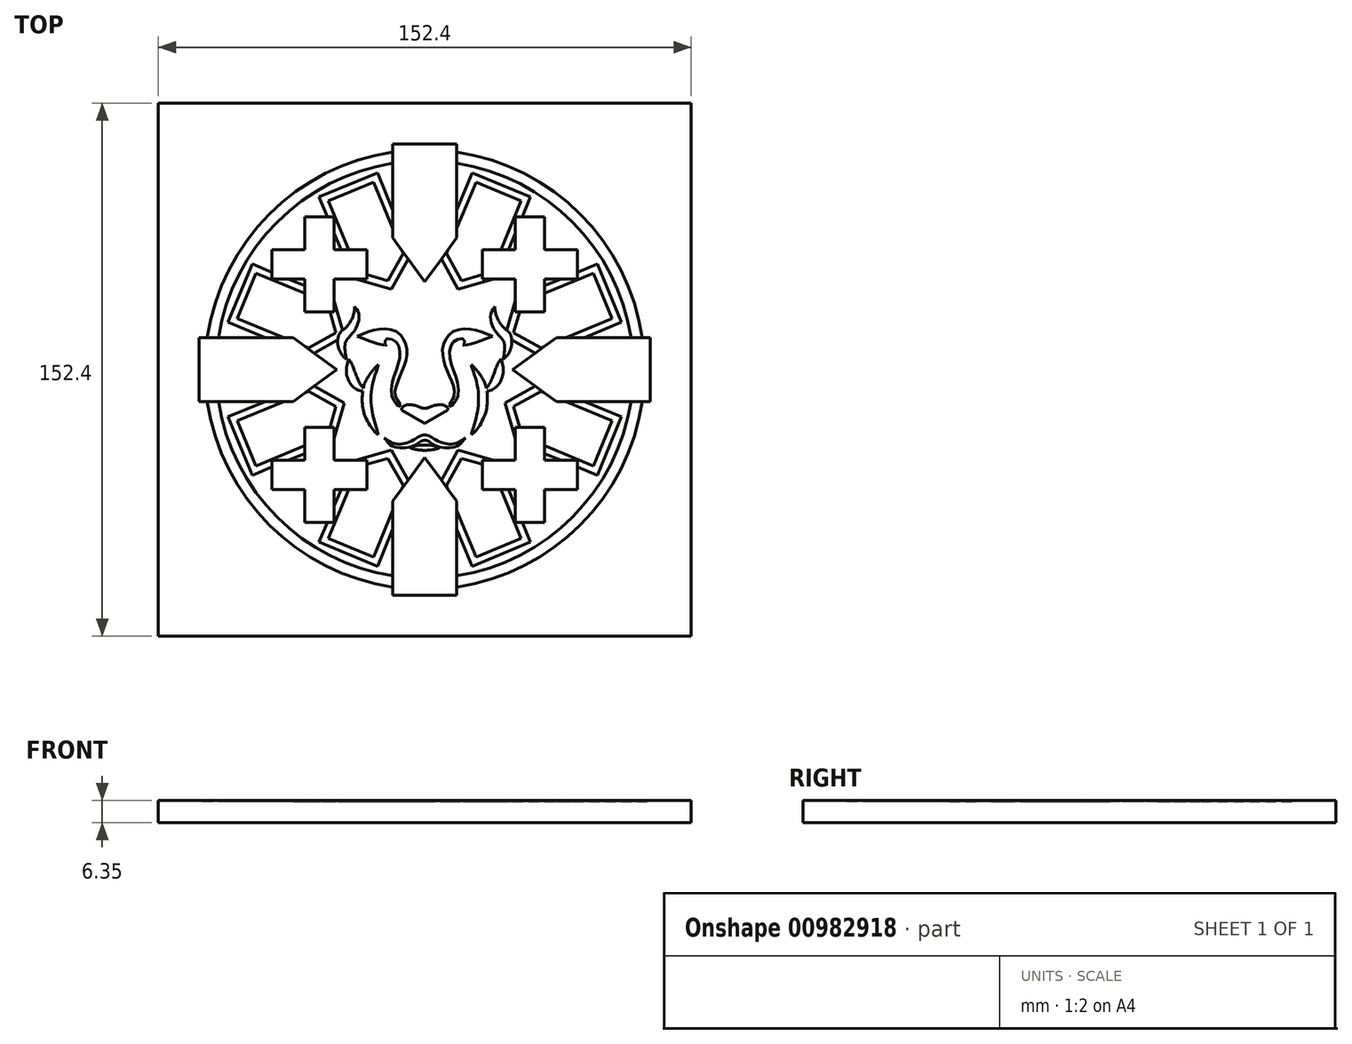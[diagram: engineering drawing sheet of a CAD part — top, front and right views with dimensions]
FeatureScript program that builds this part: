
annotation { "Feature Type Name" : "Feature", "Feature Type Description" : "" }
export const myFeature = defineFeature(function(context is Context, id is Id, definition is map)
    precondition{}
    {
        {
            assignVariable(context, id + "F0", {"name" : "depthArrowsHollow", "anyValue" : .2});
        }
        {
            assignVariable(context, id + "F1", {"name" : "depthArrowsSolid", "anyValue" : .4});
        }
        {
            assignVariable(context, id + "F2", {"name" : "depthCircle", "anyValue" : .2});
        }
        {
            assignVariable(context, id + "F3", {"name" : "depthCrosses", "anyValue" : .4});
        }
        {
            assignVariable(context, id + "F4", {"name" : "depthLion", "anyValue" : .4});
        }
        {
            var Q0;
            Q0=qCreatedBy(makeId("Top.planeOp"),FACE);
            var sketch = newSketch(context, id + "F5", { "sketchPlane" : qUnion([Q0])});
            skSolve(sketch);
        }
        {
            var Q0;
            Q0=qCreatedBy(makeId("Top.planeOp"),FACE);
            var sketch = newSketch(context, id + "F6", { "sketchPlane" : qUnion([Q0])});
            skCircle(sketch, "E0", {"center": v(81.98, 70.61) * mm, "radius": 59.7 * mm});
            skCircle(sketch, "E1", {"center": v(81.98, 70.61) * mm, "radius": 62.87 * mm});
            skPoint(sketch, "E2", {"position": v(0, 76.2) * mm});
            skPoint(sketch, "E3", {"position": v(75.25, 0) * mm});
            skLineSegment(sketch, "E4.bottom", {"start": v(5.78, -5.59) * mm, "end": v(158.18, -5.59) * mm});
            skLineSegment(sketch, "E4.top", {"start": v(5.78, 146.81) * mm, "end": v(158.18, 146.81) * mm});
            skLineSegment(sketch, "E4.left", {"start": v(5.78, -5.59) * mm, "end": v(5.78, 146.81) * mm});
            skLineSegment(sketch, "E4.right", {"start": v(158.18, -5.59) * mm, "end": v(158.18, 146.81) * mm});
            skSolve(sketch);
        }
        {
            var Q0;
            Q0=makeQuery(id+"F6.imprint","IMPRINT",FACE,{"disambiguationData":[TD([[makeQuery(id+"F6.imprint","IMPRINT",EDGE,{"derivedFrom":sQuery(id+"F6.wireOp",EDGE,"E1")}),-1.0]])]});
            var Q1;
            Q1=makeQuery(id+"F6.imprint","IMPRINT",FACE,{"disambiguationData":[TD([[makeQuery(id+"F6.imprint","IMPRINT",EDGE,{"derivedFrom":sQuery(id+"F6.wireOp",EDGE,"E0")}),-1.0]])]});
            var Q2;
            Q2=makeQuery(id+"F6.imprint","IMPRINT",FACE,{"disambiguationData":[TD([[makeQuery(id+"F6.imprint","IMPRINT",EDGE,{"derivedFrom":sQuery(id+"F6.wireOp",EDGE,"E0")}),1.0]])]});
            extrude(context, id + "F7", {"entities" : qUnion([Q0, Q1, Q2]), "oppositeDirection" : true, "depth" : 6.35 * mm, "offsetDistance" : 25.4 * mm});
        }
        {
            var Q0;
            Q0=makeQuery(id+"F6.imprint","IMPRINT",FACE,{"disambiguationData":[TD([[makeQuery(id+"F6.imprint","IMPRINT",EDGE,{"derivedFrom":sQuery(id+"F6.wireOp",EDGE,"E0")}),-1.0]])]});
            extrude(context, id + "F8", {"entities" : qUnion([Q0]), "operationType" : NewBodyOperationType.REMOVE, "oppositeDirection" : true, "depth" : (getVariable(context, 'depthCircle')) * mm, "offsetDistance" : 25.4 * mm});
        }
        {
            var Q0;
            Q0=qCreatedBy(makeId("Top.planeOp"),FACE);
            var sketch = newSketch(context, id + "F9", { "sketchPlane" : qUnion([Q0])});
            skLineSegment(sketch, "E5", {"start": v(17.47, 79.76) * mm, "end": v(17.47, 61.47) * mm});
            skLineSegment(sketch, "E6", {"start": v(17.47, 61.47) * mm, "end": v(44.33, 61.47) * mm});
            skLineSegment(sketch, "E7", {"start": v(44.33, 61.47) * mm, "end": v(56.84, 70.61) * mm});
            skLineSegment(sketch, "E8", {"start": v(56.84, 70.61) * mm, "end": v(44.33, 79.76) * mm});
            skLineSegment(sketch, "E9", {"start": v(44.33, 79.76) * mm, "end": v(17.47, 79.76) * mm});
            skCircle(sketch, "E10.0", {"center": v(81.98, 70.61) * mm, "radius": 62.87 * mm, "construction": true});
            skLineSegment(sketch, "E11", {"start": v(81.98, 70.61) * mm, "end": v(19.12, 70.61) * mm, "construction": true});
            skLineSegment(sketch, "E12.1.0", {"start": v(72.84, 32.96) * mm, "end": v(72.84, 6.1) * mm});
            skLineSegment(sketch, "E12.1.1", {"start": v(72.84, 6.1) * mm, "end": v(91.13, 6.1) * mm});
            skLineSegment(sketch, "E12.1.2", {"start": v(91.13, 6.1) * mm, "end": v(91.13, 32.96) * mm});
            skLineSegment(sketch, "E12.1.3", {"start": v(91.13, 32.96) * mm, "end": v(81.98, 45.47) * mm});
            skLineSegment(sketch, "E12.1.4", {"start": v(81.98, 45.47) * mm, "end": v(72.84, 32.96) * mm});
            skLineSegment(sketch, "E12.2.0", {"start": v(119.64, 61.47) * mm, "end": v(146.5, 61.47) * mm});
            skLineSegment(sketch, "E12.2.1", {"start": v(146.5, 61.47) * mm, "end": v(146.5, 79.76) * mm});
            skLineSegment(sketch, "E12.2.2", {"start": v(146.5, 79.76) * mm, "end": v(119.64, 79.76) * mm});
            skLineSegment(sketch, "E12.2.3", {"start": v(119.64, 79.76) * mm, "end": v(107.13, 70.61) * mm});
            skLineSegment(sketch, "E12.2.4", {"start": v(107.13, 70.61) * mm, "end": v(119.64, 61.47) * mm});
            skLineSegment(sketch, "E12.anchor1", {"start": v(81.98, 70.61) * mm, "end": v(17.47, 79.76) * mm, "construction": true});
            skLineSegment(sketch, "E12.anchor2", {"start": v(81.98, 70.61) * mm, "end": v(91.13, 135.13) * mm, "construction": true});
            skLineSegment(sketch, "E13.2.3.0", {"start": v(91.13, 108.27) * mm, "end": v(91.13, 135.13) * mm});
            skLineSegment(sketch, "E13.3.3.0", {"start": v(91.13, 135.13) * mm, "end": v(72.84, 135.13) * mm});
            skLineSegment(sketch, "E13.6.3.0", {"start": v(72.84, 135.13) * mm, "end": v(72.84, 108.27) * mm});
            skLineSegment(sketch, "E13.9.3.0", {"start": v(72.84, 108.27) * mm, "end": v(81.98, 95.76) * mm});
            skLineSegment(sketch, "E13.12.3.0", {"start": v(81.98, 95.76) * mm, "end": v(91.13, 108.27) * mm});
            skSolve(sketch);
        }
        {
            var Q0;
            Q0 = qSketchRegion(id + "F9", true);
            extrude(context, id + "F10", {"entities" : qUnion([Q0]), "operationType" : NewBodyOperationType.REMOVE, "oppositeDirection" : true, "depth" : (getVariable(context, 'depthArrowsSolid')) * mm, "offsetDistance" : 25.4 * mm});
        }
        {
            var Q0;
            Q0=qCreatedBy(makeId("Top.planeOp"),FACE);
            var sketch = newSketch(context, id + "F11", { "sketchPlane" : qUnion([Q0])});
            skLineSegment(sketch, "E14", {"start": v(47.7, 54.1) * mm, "end": v(56.07, 54.1) * mm});
            skLineSegment(sketch, "E15", {"start": v(56.07, 54.1) * mm, "end": v(56.07, 44.7) * mm});
            skLineSegment(sketch, "E16", {"start": v(56.07, 44.7) * mm, "end": v(65.47, 44.7) * mm});
            skLineSegment(sketch, "E17", {"start": v(65.47, 44.7) * mm, "end": v(65.47, 36.32) * mm});
            skLineSegment(sketch, "E18", {"start": v(65.47, 36.32) * mm, "end": v(56.07, 36.32) * mm});
            skLineSegment(sketch, "E19", {"start": v(56.07, 36.32) * mm, "end": v(56.07, 26.92) * mm});
            skLineSegment(sketch, "E20", {"start": v(56.07, 26.92) * mm, "end": v(47.7, 26.92) * mm});
            skLineSegment(sketch, "E21", {"start": v(47.7, 26.92) * mm, "end": v(47.7, 36.32) * mm});
            skLineSegment(sketch, "E22", {"start": v(47.7, 36.32) * mm, "end": v(38.3, 36.32) * mm});
            skLineSegment(sketch, "E23", {"start": v(38.3, 36.32) * mm, "end": v(38.3, 44.7) * mm});
            skLineSegment(sketch, "E24", {"start": v(38.3, 44.7) * mm, "end": v(47.7, 44.7) * mm});
            skLineSegment(sketch, "E25", {"start": v(47.7, 44.7) * mm, "end": v(47.7, 54.1) * mm});
            skCircle(sketch, "E26.0", {"center": v(81.98, 70.61) * mm, "radius": 62.87 * mm, "construction": true});
            skLineSegment(sketch, "E27.1.0", {"start": v(107.89, 26.92) * mm, "end": v(107.89, 36.32) * mm});
            skLineSegment(sketch, "E27.1.1", {"start": v(98.5, 36.32) * mm, "end": v(98.5, 44.7) * mm});
            skLineSegment(sketch, "E27.1.2", {"start": v(107.89, 44.7) * mm, "end": v(107.89, 54.1) * mm});
            skLineSegment(sketch, "E27.1.3", {"start": v(116.27, 54.1) * mm, "end": v(116.27, 44.7) * mm});
            skLineSegment(sketch, "E27.1.4", {"start": v(116.27, 36.32) * mm, "end": v(116.27, 26.92) * mm});
            skLineSegment(sketch, "E27.1.5", {"start": v(125.67, 44.7) * mm, "end": v(125.67, 36.32) * mm});
            skLineSegment(sketch, "E27.1.6", {"start": v(125.67, 36.32) * mm, "end": v(116.27, 36.32) * mm});
            skLineSegment(sketch, "E27.1.7", {"start": v(116.27, 44.7) * mm, "end": v(125.67, 44.7) * mm});
            skLineSegment(sketch, "E27.1.8", {"start": v(116.27, 26.92) * mm, "end": v(107.89, 26.92) * mm});
            skLineSegment(sketch, "E27.1.9", {"start": v(107.89, 54.1) * mm, "end": v(116.27, 54.1) * mm});
            skLineSegment(sketch, "E27.1.10", {"start": v(98.5, 44.7) * mm, "end": v(107.89, 44.7) * mm});
            skLineSegment(sketch, "E27.1.11", {"start": v(107.89, 36.32) * mm, "end": v(98.5, 36.32) * mm});
            skLineSegment(sketch, "E27.2.0", {"start": v(125.67, 96.52) * mm, "end": v(116.27, 96.52) * mm});
            skLineSegment(sketch, "E27.2.1", {"start": v(116.27, 87.12) * mm, "end": v(107.89, 87.12) * mm});
            skLineSegment(sketch, "E27.2.2", {"start": v(107.89, 96.52) * mm, "end": v(98.5, 96.52) * mm});
            skLineSegment(sketch, "E27.2.3", {"start": v(98.5, 104.9) * mm, "end": v(107.89, 104.9) * mm});
            skLineSegment(sketch, "E27.2.4", {"start": v(116.27, 104.9) * mm, "end": v(125.67, 104.9) * mm});
            skLineSegment(sketch, "E27.2.5", {"start": v(107.89, 114.3) * mm, "end": v(116.27, 114.3) * mm});
            skLineSegment(sketch, "E27.2.6", {"start": v(116.27, 114.3) * mm, "end": v(116.27, 104.9) * mm});
            skLineSegment(sketch, "E27.2.7", {"start": v(107.89, 104.9) * mm, "end": v(107.89, 114.3) * mm});
            skLineSegment(sketch, "E27.2.8", {"start": v(125.67, 104.9) * mm, "end": v(125.67, 96.52) * mm});
            skLineSegment(sketch, "E27.2.9", {"start": v(98.5, 96.52) * mm, "end": v(98.5, 104.9) * mm});
            skLineSegment(sketch, "E27.2.10", {"start": v(107.89, 87.12) * mm, "end": v(107.89, 96.52) * mm});
            skLineSegment(sketch, "E27.2.11", {"start": v(116.27, 96.52) * mm, "end": v(116.27, 87.12) * mm});
            skLineSegment(sketch, "E28.1.3.0", {"start": v(56.07, 114.3) * mm, "end": v(56.07, 104.9) * mm});
            skLineSegment(sketch, "E28.3.3.0", {"start": v(65.47, 104.9) * mm, "end": v(65.47, 96.52) * mm});
            skLineSegment(sketch, "E28.6.3.0", {"start": v(56.07, 96.52) * mm, "end": v(56.07, 87.12) * mm});
            skLineSegment(sketch, "E28.9.3.0", {"start": v(47.7, 87.12) * mm, "end": v(47.7, 96.52) * mm});
            skLineSegment(sketch, "E28.12.3.0", {"start": v(47.7, 104.9) * mm, "end": v(47.7, 114.3) * mm});
            skLineSegment(sketch, "E28.15.3.0", {"start": v(38.3, 96.52) * mm, "end": v(38.3, 104.9) * mm});
            skLineSegment(sketch, "E28.18.3.0", {"start": v(38.3, 104.9) * mm, "end": v(47.7, 104.9) * mm});
            skLineSegment(sketch, "E28.21.3.0", {"start": v(47.7, 96.52) * mm, "end": v(38.3, 96.52) * mm});
            skLineSegment(sketch, "E28.24.3.0", {"start": v(47.7, 114.3) * mm, "end": v(56.07, 114.3) * mm});
            skLineSegment(sketch, "E28.27.3.0", {"start": v(56.07, 87.12) * mm, "end": v(47.7, 87.12) * mm});
            skLineSegment(sketch, "E28.30.3.0", {"start": v(65.47, 96.52) * mm, "end": v(56.07, 96.52) * mm});
            skLineSegment(sketch, "E28.33.3.0", {"start": v(56.07, 104.9) * mm, "end": v(65.47, 104.9) * mm});
            skSolve(sketch);
        }
        {
            var Q0;
            Q0=makeQuery(id+"F11.imprint","IMPRINT",FACE,{"disambiguationData":[TD([[makeQuery(id+"F11.imprint","IMPRINT",EDGE,{"derivedFrom":sQuery(id+"F11.wireOp",EDGE,"E28.1.3.0")}),-1.0]])]});
            var Q1;
            Q1=makeQuery(id+"F11.imprint","IMPRINT",FACE,{"disambiguationData":[TD([[makeQuery(id+"F11.imprint","IMPRINT",EDGE,{"derivedFrom":sQuery(id+"F11.wireOp",EDGE,"E27.2.0")}),-1.0]])]});
            var Q2;
            Q2=makeQuery(id+"F11.imprint","IMPRINT",FACE,{"disambiguationData":[TD([[makeQuery(id+"F11.imprint","IMPRINT",EDGE,{"derivedFrom":sQuery(id+"F11.wireOp",EDGE,"E27.1.0")}),-1.0]])]});
            var Q3;
            Q3=makeQuery(id+"F11.imprint","IMPRINT",FACE,{"disambiguationData":[TD([[makeQuery(id+"F11.imprint","IMPRINT",EDGE,{"derivedFrom":sQuery(id+"F11.wireOp",EDGE,"E14")}),-1.0]])]});
            var Q4;
            Q4=makeQuery(id+"F9.imprint","IMPRINT",FACE,{"disambiguationData":[TD([[makeQuery(id+"F9.imprint","IMPRINT",EDGE,{"derivedFrom":sQuery(id+"F9.wireOp",EDGE,"E5")}),1.0]])]});
            var Q5;
            Q5=makeQuery(id+"F9.imprint","IMPRINT",FACE,{"disambiguationData":[TD([[makeQuery(id+"F9.imprint","IMPRINT",EDGE,{"derivedFrom":sQuery(id+"F9.wireOp",EDGE,"E13.2.3.0")}),1.0]])]});
            var Q6;
            Q6=makeQuery(id+"F9.imprint","IMPRINT",FACE,{"disambiguationData":[TD([[makeQuery(id+"F9.imprint","IMPRINT",EDGE,{"derivedFrom":sQuery(id+"F9.wireOp",EDGE,"E12.2.0")}),1.0]])]});
            var Q7;
            Q7=makeQuery(id+"F9.imprint","IMPRINT",FACE,{"disambiguationData":[TD([[makeQuery(id+"F9.imprint","IMPRINT",EDGE,{"derivedFrom":sQuery(id+"F9.wireOp",EDGE,"E12.1.0")}),1.0]])]});
            extrude(context, id + "F12", {"entities" : qUnion([Q0, Q1, Q2, Q3, Q4, Q5, Q6, Q7]), "operationType" : NewBodyOperationType.REMOVE, "oppositeDirection" : true, "depth" : (getVariable(context, 'depthCrosses')) * mm, "offsetDistance" : 25.4 * mm});
        }
        {
            var Q0;
            Q0=qCreatedBy(makeId("Top.planeOp"),FACE);
            var sketch = newSketch(context, id + "F13", { "sketchPlane" : qUnion([Q0])});
            skLineSegment(sketch, "E29", {"start": v(25.73, 57.07) * mm, "end": v(48.9, 66.67) * mm});
            skLineSegment(sketch, "E30", {"start": v(48.9, 66.67) * mm, "end": v(58.98, 61.09) * mm});
            skLineSegment(sketch, "E31", {"start": v(58.98, 61.09) * mm, "end": v(55.8, 50.01) * mm});
            skLineSegment(sketch, "E32", {"start": v(55.8, 50.01) * mm, "end": v(32.63, 40.41) * mm});
            skLineSegment(sketch, "E33", {"start": v(32.63, 40.41) * mm, "end": v(25.73, 57.07) * mm});
            skCircle(sketch, "E34.0", {"center": v(81.98, 70.61) * mm, "radius": 62.87 * mm, "construction": true});
            skLineSegment(sketch, "E35", {"start": v(81.98, 70.61) * mm, "end": v(29.18, 48.74) * mm, "construction": true});
            skLineSegment(sketch, "E36", {"start": v(81.98, 70.61) * mm, "end": v(19.12, 70.61) * mm, "construction": true});
            skLineSegment(sketch, "E37.0", {"start": v(48.78, 64.42) * mm, "end": v(56.59, 60.1) * mm});
            skLineSegment(sketch, "E37.1", {"start": v(28.39, 55.97) * mm, "end": v(48.78, 64.42) * mm});
            skLineSegment(sketch, "E37.2", {"start": v(56.59, 60.1) * mm, "end": v(54.13, 51.51) * mm});
            skLineSegment(sketch, "E37.3", {"start": v(54.13, 51.51) * mm, "end": v(33.73, 43.07) * mm});
            skLineSegment(sketch, "E37.4", {"start": v(33.73, 43.07) * mm, "end": v(28.39, 55.97) * mm});
            skLineSegment(sketch, "E38.1.0", {"start": v(54.44, 22.36) * mm, "end": v(62.88, 42.76) * mm});
            skLineSegment(sketch, "E38.1.1", {"start": v(51.78, 21.26) * mm, "end": v(61.38, 44.44) * mm});
            skLineSegment(sketch, "E38.1.2", {"start": v(75.79, 37.4) * mm, "end": v(67.34, 17.02) * mm});
            skLineSegment(sketch, "E38.1.3", {"start": v(78.04, 37.54) * mm, "end": v(68.44, 14.36) * mm});
            skLineSegment(sketch, "E38.1.4", {"start": v(67.34, 17.02) * mm, "end": v(54.44, 22.36) * mm});
            skLineSegment(sketch, "E38.1.5", {"start": v(68.44, 14.36) * mm, "end": v(51.78, 21.26) * mm});
            skLineSegment(sketch, "E38.1.6", {"start": v(62.88, 42.76) * mm, "end": v(71.46, 45.22) * mm});
            skLineSegment(sketch, "E38.1.7", {"start": v(61.38, 44.44) * mm, "end": v(72.46, 47.61) * mm});
            skLineSegment(sketch, "E38.1.8", {"start": v(71.46, 45.22) * mm, "end": v(75.79, 37.4) * mm});
            skLineSegment(sketch, "E38.1.9", {"start": v(72.46, 47.61) * mm, "end": v(78.04, 37.54) * mm});
            skLineSegment(sketch, "E38.2.0", {"start": v(96.62, 17.02) * mm, "end": v(88.17, 37.4) * mm});
            skLineSegment(sketch, "E38.2.1", {"start": v(95.52, 14.36) * mm, "end": v(85.92, 37.54) * mm});
            skLineSegment(sketch, "E38.2.2", {"start": v(101.08, 42.76) * mm, "end": v(109.53, 22.36) * mm});
            skLineSegment(sketch, "E38.2.3", {"start": v(102.58, 44.44) * mm, "end": v(112.18, 21.26) * mm});
            skLineSegment(sketch, "E38.2.4", {"start": v(109.53, 22.36) * mm, "end": v(96.62, 17.02) * mm});
            skLineSegment(sketch, "E38.2.5", {"start": v(112.18, 21.26) * mm, "end": v(95.52, 14.36) * mm});
            skLineSegment(sketch, "E38.2.6", {"start": v(88.17, 37.4) * mm, "end": v(92.5, 45.22) * mm});
            skLineSegment(sketch, "E38.2.7", {"start": v(85.92, 37.54) * mm, "end": v(91.5, 47.61) * mm});
            skLineSegment(sketch, "E38.2.8", {"start": v(92.5, 45.22) * mm, "end": v(101.08, 42.76) * mm});
            skLineSegment(sketch, "E38.2.9", {"start": v(91.5, 47.61) * mm, "end": v(102.58, 44.44) * mm});
            skLineSegment(sketch, "E39.1.3.0", {"start": v(130.23, 43.07) * mm, "end": v(109.84, 51.51) * mm});
            skLineSegment(sketch, "E39.3.3.0", {"start": v(131.33, 40.41) * mm, "end": v(108.15, 50.01) * mm});
            skLineSegment(sketch, "E39.6.3.0", {"start": v(115.18, 64.42) * mm, "end": v(135.58, 55.97) * mm});
            skLineSegment(sketch, "E39.9.3.0", {"start": v(115.06, 66.67) * mm, "end": v(138.23, 57.07) * mm});
            skLineSegment(sketch, "E39.12.3.0", {"start": v(135.58, 55.97) * mm, "end": v(130.23, 43.07) * mm});
            skLineSegment(sketch, "E39.15.3.0", {"start": v(138.23, 57.07) * mm, "end": v(131.33, 40.41) * mm});
            skLineSegment(sketch, "E39.18.3.0", {"start": v(109.84, 51.51) * mm, "end": v(107.38, 60.1) * mm});
            skLineSegment(sketch, "E39.21.3.0", {"start": v(108.15, 50.01) * mm, "end": v(104.98, 61.09) * mm});
            skLineSegment(sketch, "E39.24.3.0", {"start": v(107.38, 60.1) * mm, "end": v(115.18, 64.42) * mm});
            skLineSegment(sketch, "E39.27.3.0", {"start": v(104.98, 61.09) * mm, "end": v(115.06, 66.67) * mm});
            skLineSegment(sketch, "E39.1.4.0", {"start": v(135.58, 85.25) * mm, "end": v(115.18, 76.8) * mm});
            skLineSegment(sketch, "E39.3.4.0", {"start": v(138.23, 84.15) * mm, "end": v(115.06, 74.55) * mm});
            skLineSegment(sketch, "E39.6.4.0", {"start": v(109.84, 89.71) * mm, "end": v(130.23, 98.16) * mm});
            skLineSegment(sketch, "E39.9.4.0", {"start": v(108.15, 91.21) * mm, "end": v(131.33, 100.81) * mm});
            skLineSegment(sketch, "E39.12.4.0", {"start": v(130.23, 98.16) * mm, "end": v(135.58, 85.25) * mm});
            skLineSegment(sketch, "E39.15.4.0", {"start": v(131.33, 100.81) * mm, "end": v(138.23, 84.15) * mm});
            skLineSegment(sketch, "E39.18.4.0", {"start": v(115.18, 76.8) * mm, "end": v(107.38, 81.13) * mm});
            skLineSegment(sketch, "E39.21.4.0", {"start": v(115.06, 74.55) * mm, "end": v(104.98, 80.14) * mm});
            skLineSegment(sketch, "E39.24.4.0", {"start": v(107.38, 81.13) * mm, "end": v(109.84, 89.71) * mm});
            skLineSegment(sketch, "E39.27.4.0", {"start": v(104.98, 80.14) * mm, "end": v(108.15, 91.21) * mm});
            skLineSegment(sketch, "E39.1.5.0", {"start": v(109.53, 118.86) * mm, "end": v(101.08, 98.47) * mm});
            skLineSegment(sketch, "E39.3.5.0", {"start": v(112.18, 119.96) * mm, "end": v(102.58, 96.79) * mm});
            skLineSegment(sketch, "E39.6.5.0", {"start": v(88.17, 103.81) * mm, "end": v(96.62, 124.2) * mm});
            skLineSegment(sketch, "E39.9.5.0", {"start": v(85.92, 103.69) * mm, "end": v(95.52, 126.86) * mm});
            skLineSegment(sketch, "E39.12.5.0", {"start": v(96.62, 124.2) * mm, "end": v(109.53, 118.86) * mm});
            skLineSegment(sketch, "E39.15.5.0", {"start": v(95.52, 126.86) * mm, "end": v(112.18, 119.96) * mm});
            skLineSegment(sketch, "E39.18.5.0", {"start": v(101.08, 98.47) * mm, "end": v(92.5, 96) * mm});
            skLineSegment(sketch, "E39.21.5.0", {"start": v(102.58, 96.79) * mm, "end": v(91.5, 93.6) * mm});
            skLineSegment(sketch, "E39.24.5.0", {"start": v(92.5, 96) * mm, "end": v(88.17, 103.81) * mm});
            skLineSegment(sketch, "E39.27.5.0", {"start": v(91.5, 93.6) * mm, "end": v(85.92, 103.69) * mm});
            skLineSegment(sketch, "E39.1.6.0", {"start": v(67.34, 124.2) * mm, "end": v(75.79, 103.81) * mm});
            skLineSegment(sketch, "E39.3.6.0", {"start": v(68.44, 126.86) * mm, "end": v(78.04, 103.69) * mm});
            skLineSegment(sketch, "E39.6.6.0", {"start": v(62.88, 98.47) * mm, "end": v(54.44, 118.86) * mm});
            skLineSegment(sketch, "E39.9.6.0", {"start": v(61.38, 96.79) * mm, "end": v(51.78, 119.96) * mm});
            skLineSegment(sketch, "E39.12.6.0", {"start": v(54.44, 118.86) * mm, "end": v(67.34, 124.2) * mm});
            skLineSegment(sketch, "E39.15.6.0", {"start": v(51.78, 119.96) * mm, "end": v(68.44, 126.86) * mm});
            skLineSegment(sketch, "E39.18.6.0", {"start": v(75.79, 103.81) * mm, "end": v(71.46, 96) * mm});
            skLineSegment(sketch, "E39.21.6.0", {"start": v(78.04, 103.69) * mm, "end": v(72.46, 93.6) * mm});
            skLineSegment(sketch, "E39.24.6.0", {"start": v(71.46, 96) * mm, "end": v(62.88, 98.47) * mm});
            skLineSegment(sketch, "E39.27.6.0", {"start": v(72.46, 93.6) * mm, "end": v(61.38, 96.79) * mm});
            skLineSegment(sketch, "E39.1.7.0", {"start": v(33.73, 98.16) * mm, "end": v(54.13, 89.71) * mm});
            skLineSegment(sketch, "E39.3.7.0", {"start": v(32.63, 100.81) * mm, "end": v(55.8, 91.21) * mm});
            skLineSegment(sketch, "E39.6.7.0", {"start": v(48.78, 76.8) * mm, "end": v(28.39, 85.25) * mm});
            skLineSegment(sketch, "E39.9.7.0", {"start": v(48.9, 74.55) * mm, "end": v(25.73, 84.15) * mm});
            skLineSegment(sketch, "E39.12.7.0", {"start": v(28.39, 85.25) * mm, "end": v(33.73, 98.16) * mm});
            skLineSegment(sketch, "E39.15.7.0", {"start": v(25.73, 84.15) * mm, "end": v(32.63, 100.81) * mm});
            skLineSegment(sketch, "E39.18.7.0", {"start": v(54.13, 89.71) * mm, "end": v(56.59, 81.13) * mm});
            skLineSegment(sketch, "E39.21.7.0", {"start": v(55.8, 91.21) * mm, "end": v(58.98, 80.14) * mm});
            skLineSegment(sketch, "E39.24.7.0", {"start": v(56.59, 81.13) * mm, "end": v(48.78, 76.8) * mm});
            skLineSegment(sketch, "E39.27.7.0", {"start": v(58.98, 80.14) * mm, "end": v(48.9, 74.55) * mm});
            skSolve(sketch);
        }
        {
            var Q0;
            Q0 = qSketchRegion(id + "F13", true);
            extrude(context, id + "F14", {"entities" : qUnion([Q0]), "operationType" : NewBodyOperationType.REMOVE, "oppositeDirection" : true, "depth" : (getVariable(context, 'depthArrowsHollow')) * mm, "offsetDistance" : 25.4 * mm});
        }
        {
            var Q0;
            Q0=qCreatedBy(makeId("Top.planeOp"),FACE);
            var sketch = newSketch(context, id + "F15", { "sketchPlane" : qUnion([Q0])});
            skLineSegment(sketch, "E40", {"start": v(81.98, 146.81) * mm, "end": v(81.98, -5.59) * mm, "construction": true});
            skFitSpline(sketch, "E41", {"points": [v(61.94, 88.6) * mm, v(61.72, 86.72) * mm, v(61.16, 85.16) * mm, v(60.37, 83.77) * mm, v(59.24, 82.46) * mm, v(57.86, 81.25) * mm, v(57.15, 79.47) * mm, v(57.17, 77.48) * mm, v(58.02, 75.2) * mm, v(59.6, 73.57) * mm], "startDerivative": vector(0.03, -23.03) * mm, "endDerivative": vector(20.52, -14.62) * mm});
            skFitSpline(sketch, "E42", {"points": [v(61.94, 88.6) * mm, v(63.17, 85.4) * mm, v(61.82, 81.66) * mm, v(59.62, 79.03) * mm, v(59.15, 77.49) * mm, v(59.2, 75.8) * mm, v(59.6, 73.57) * mm], "startDerivative": vector(15.35, -14.7) * mm, "endDerivative": vector(4.08, -12.06) * mm});
            skFitSpline(sketch, "E43", {"points": [v(60.19, 73.61) * mm, v(59.65, 71.61) * mm, v(59.62, 69.33) * mm, v(60.38, 67.13) * mm, v(61.9, 65.3) * mm, v(63.68, 64.54) * mm, v(65.16, 64.56) * mm], "startDerivative": vector(-2.41, -6.85) * mm, "endDerivative": vector(6.9, 1.88) * mm});
            skFitSpline(sketch, "E44", {"points": [v(60.19, 73.61) * mm, v(60.88, 72.65) * mm, v(61.49, 71.36) * mm, v(62.1, 69.66) * mm, v(62.83, 67.93) * mm, v(63.58, 66.36) * mm, v(64.31, 65.39) * mm, v(65.16, 64.56) * mm], "startDerivative": vector(5.66, -7.2) * mm, "endDerivative": vector(1.92, -1.83) * mm});
            skFitSpline(sketch, "E45", {"points": [v(62.61, 80.06) * mm, v(65.49, 81.37) * mm, v(68.65, 82.13) * mm, v(71.55, 82.19) * mm, v(74.34, 81.17) * mm, v(75.9, 79.37) * mm, v(76.8, 77.03) * mm, v(76.77, 74.1) * mm, v(76, 71.47) * mm, v(74.87, 68.71) * mm, v(73.97, 66.34) * mm, v(73.44, 64.03) * mm, v(74.08, 61.94) * mm, v(74.86, 60.7) * mm, v(74.91, 60.03) * mm], "startDerivative": vector(34.56, 17.51) * mm, "endDerivative": vector(-4.35, -17.1) * mm});
            skFitSpline(sketch, "E46", {"points": [v(74.91, 60.03) * mm, v(74.28, 60.16) * mm, v(73.28, 61.53) * mm, v(72.44, 63.44) * mm, v(72.55, 66.35) * mm, v(73.32, 69.02) * mm, v(74.22, 71.68) * mm, v(74.84, 74.24) * mm, v(74.73, 76.7) * mm, v(74.03, 78.22) * mm, v(72.94, 79.03) * mm, v(71.18, 79.46) * mm, v(70.7, 78.99) * mm, v(70.58, 78.47) * mm, v(70.7, 77.97) * mm, v(70.9, 77.62) * mm, v(70.93, 77.54) * mm, v(70.82, 77.54) * mm, v(69.56, 77.7) * mm, v(68.42, 78) * mm, v(67.1, 78.45) * mm, v(65.18, 79.17) * mm, v(62.61, 80.06) * mm], "startDerivative": vector(-21.39, -1.32) * mm, "endDerivative": vector(-39.34, 13.04) * mm});
            skFitSpline(sketch, "E47", {"points": [v(68.72, 72) * mm, v(68.33, 70.7) * mm, v(67.57, 68.42) * mm, v(66.9, 65.8) * mm, v(66.58, 62.86) * mm, v(66.73, 60.18) * mm, v(67.07, 57.9) * mm, v(67.64, 55.51) * mm, v(68.31, 53.3) * mm, v(68.71, 52) * mm], "startDerivative": vector(-6.69, -19.51) * mm, "endDerivative": vector(4.6, -12.75) * mm});
            skFitSpline(sketch, "E48", {"points": [v(68.71, 52) * mm, v(67.56, 52.94) * mm, v(65.3, 56.48) * mm, v(64.22, 59.9) * mm, v(64.12, 63.32) * mm, v(64.79, 66.64) * mm, v(66.23, 69.26) * mm, v(67.6, 71) * mm, v(68.72, 72) * mm], "startDerivative": vector(-13.48, 8.73) * mm, "endDerivative": vector(15.01, 11.43) * mm});
            skFitSpline(sketch, "E49", {"points": [v(70.36, 51.06) * mm, v(70.67, 50.78) * mm, v(70.99, 50.37) * mm, v(71.26, 49.96) * mm, v(71.6, 49.53) * mm, v(72.75, 48.76) * mm, v(74.23, 48.32) * mm, v(76.3, 48.28) * mm, v(78.03, 48.59) * mm, v(79.36, 49.08) * mm, v(80.25, 49.7) * mm, v(80.77, 50.1) * mm, v(81.26, 50.3) * mm, v(81.68, 50.34) * mm, v(81.98, 50.34) * mm], "startDerivative": vector(6.26, -5.13) * mm, "endDerivative": vector(6.83, -0.1) * mm});
            skFitSpline(sketch, "E50", {"points": [v(70.36, 51.06) * mm, v(70.75, 50.83) * mm, v(71.26, 50.5) * mm, v(72.1, 50) * mm, v(73, 49.58) * mm, v(74.2, 49.32) * mm, v(75.52, 49.35) * mm, v(77.03, 49.74) * mm, v(78.68, 50.44) * mm, v(79.85, 51.2) * mm, v(80.76, 51.7) * mm, v(81.5, 51.89) * mm, v(81.98, 51.9) * mm], "startDerivative": vector(6.78, -3.92) * mm, "endDerivative": vector(7.94, 0.08) * mm});
            skFitSpline(sketch, "E51", {"points": [v(75.37, 59.05) * mm, v(75.43, 59.4) * mm, v(75.72, 59.93) * mm, v(76.23, 60.35) * mm, v(77.07, 60.53) * mm, v(78.5, 60.5) * mm, v(79.56, 60.28) * mm, v(80.47, 59.92) * mm, v(81.08, 59.67) * mm, v(81.55, 59.56) * mm, v(81.98, 59.55) * mm], "startDerivative": vector(0.5, 4.55) * mm, "endDerivative": vector(5.33, 0.06) * mm});
            skLineSegment(sketch, "E52", {"start": v(75.37, 59.05) * mm, "end": v(81.98, 55.18) * mm});
            skFitSpline(sketch, "E53", {"points": [v(77.74, 48.25) * mm, v(78.08, 48.39) * mm, v(79.03, 48.72) * mm, v(80.05, 48.95) * mm, v(81.12, 49.04) * mm, v(81.98, 49.03) * mm], "startDerivative": vector(2.37, 1.14) * mm, "endDerivative": vector(4.16, -0.05) * mm});
            skFitSpline(sketch, "E54", {"points": [v(77.74, 48.25) * mm, v(78.13, 48.1) * mm, v(78.98, 47.86) * mm, v(79.86, 47.7) * mm, v(80.82, 47.6) * mm, v(81.6, 47.52) * mm, v(81.98, 47.5) * mm], "startDerivative": vector(2.66, -1.22) * mm, "endDerivative": vector(2.55, -0.14) * mm});
            skFitSpline(sketch, "E55.MirrorCS", {"points": [v(86.22, 48.25) * mm, v(85.89, 48.39) * mm, v(84.93, 48.72) * mm, v(83.91, 48.95) * mm, v(82.85, 49.04) * mm, v(81.98, 49.03) * mm], "startDerivative": vector(-2.37, 1.14) * mm, "endDerivative": vector(-4.16, -0.05) * mm});
            skFitSpline(sketch, "E56.MirrorCS", {"points": [v(86.22, 48.25) * mm, v(85.84, 48.1) * mm, v(84.98, 47.86) * mm, v(84.1, 47.7) * mm, v(83.14, 47.6) * mm, v(82.37, 47.52) * mm, v(81.98, 47.5) * mm], "startDerivative": vector(-2.66, -1.22) * mm, "endDerivative": vector(-2.55, -0.14) * mm});
            skFitSpline(sketch, "E57.MirrorCS", {"points": [v(88.59, 59.05) * mm, v(88.53, 59.4) * mm, v(88.24, 59.93) * mm, v(87.73, 60.35) * mm, v(86.9, 60.53) * mm, v(85.45, 60.5) * mm, v(84.4, 60.28) * mm, v(83.5, 59.92) * mm, v(82.88, 59.67) * mm, v(82.41, 59.56) * mm, v(81.98, 59.55) * mm], "startDerivative": vector(-0.5, 4.55) * mm, "endDerivative": vector(-5.33, 0.06) * mm});
            skFitSpline(sketch, "E58.MirrorCS", {"points": [v(93.6, 51.06) * mm, v(93.22, 50.83) * mm, v(92.7, 50.5) * mm, v(91.87, 50) * mm, v(90.97, 49.58) * mm, v(89.77, 49.32) * mm, v(88.44, 49.35) * mm, v(86.94, 49.74) * mm, v(85.28, 50.44) * mm, v(84.1, 51.2) * mm, v(83.2, 51.7) * mm, v(82.47, 51.89) * mm, v(81.98, 51.9) * mm], "startDerivative": vector(-6.78, -3.92) * mm, "endDerivative": vector(-7.94, 0.08) * mm});
            skFitSpline(sketch, "E59.MirrorCS", {"points": [v(93.6, 51.06) * mm, v(93.3, 50.78) * mm, v(92.98, 50.37) * mm, v(92.7, 49.96) * mm, v(92.37, 49.53) * mm, v(91.22, 48.76) * mm, v(89.74, 48.32) * mm, v(87.66, 48.28) * mm, v(85.93, 48.59) * mm, v(84.6, 49.08) * mm, v(83.71, 49.7) * mm, v(83.19, 50.1) * mm, v(82.7, 50.3) * mm, v(82.28, 50.34) * mm, v(81.98, 50.34) * mm], "startDerivative": vector(-6.26, -5.13) * mm, "endDerivative": vector(-6.83, -0.1) * mm});
            skFitSpline(sketch, "E60.MirrorCS", {"points": [v(102.03, 88.6) * mm, v(102.24, 86.72) * mm, v(102.8, 85.16) * mm, v(103.6, 83.77) * mm, v(104.73, 82.46) * mm, v(106.1, 81.25) * mm, v(106.81, 79.47) * mm, v(106.8, 77.48) * mm, v(105.94, 75.2) * mm, v(104.36, 73.57) * mm], "startDerivative": vector(-0.03, -23.03) * mm, "endDerivative": vector(-20.52, -14.62) * mm});
            skFitSpline(sketch, "E61.MirrorCS", {"points": [v(89.05, 60.03) * mm, v(89.68, 60.16) * mm, v(90.69, 61.53) * mm, v(91.52, 63.44) * mm, v(91.41, 66.35) * mm, v(90.64, 69.02) * mm, v(89.74, 71.68) * mm, v(89.13, 74.24) * mm, v(89.23, 76.7) * mm, v(89.93, 78.22) * mm, v(91.03, 79.03) * mm, v(92.78, 79.46) * mm, v(93.27, 78.99) * mm, v(93.38, 78.47) * mm, v(93.27, 77.97) * mm, v(93.07, 77.62) * mm, v(93.03, 77.54) * mm, v(93.15, 77.54) * mm, v(94.4, 77.7) * mm, v(95.55, 78) * mm, v(96.85, 78.45) * mm, v(98.79, 79.17) * mm, v(101.35, 80.06) * mm], "startDerivative": vector(21.39, -1.32) * mm, "endDerivative": vector(39.34, 13.04) * mm});
            skFitSpline(sketch, "E62.MirrorCS", {"points": [v(103.77, 73.61) * mm, v(103.08, 72.65) * mm, v(102.48, 71.36) * mm, v(101.86, 69.66) * mm, v(101.13, 67.93) * mm, v(100.38, 66.36) * mm, v(99.65, 65.39) * mm, v(98.8, 64.56) * mm], "startDerivative": vector(-5.66, -7.2) * mm, "endDerivative": vector(-1.92, -1.83) * mm});
            skFitSpline(sketch, "E63.MirrorCS", {"points": [v(103.77, 73.61) * mm, v(104.31, 71.61) * mm, v(104.34, 69.33) * mm, v(103.58, 67.13) * mm, v(102.06, 65.3) * mm, v(100.28, 64.54) * mm, v(98.8, 64.56) * mm], "startDerivative": vector(2.41, -6.85) * mm, "endDerivative": vector(-6.9, 1.88) * mm});
            skFitSpline(sketch, "E64.MirrorCS", {"points": [v(101.35, 80.06) * mm, v(98.48, 81.37) * mm, v(95.32, 82.13) * mm, v(92.41, 82.19) * mm, v(89.62, 81.17) * mm, v(88.07, 79.37) * mm, v(87.16, 77.03) * mm, v(87.2, 74.1) * mm, v(87.95, 71.47) * mm, v(89.1, 68.71) * mm, v(90, 66.34) * mm, v(90.53, 64.03) * mm, v(89.88, 61.94) * mm, v(89.1, 60.7) * mm, v(89.05, 60.03) * mm], "startDerivative": vector(-34.56, 17.51) * mm, "endDerivative": vector(4.35, -17.1) * mm});
            skFitSpline(sketch, "E65.MirrorCS", {"points": [v(95.24, 72) * mm, v(95.63, 70.7) * mm, v(96.4, 68.42) * mm, v(97.07, 65.8) * mm, v(97.38, 62.86) * mm, v(97.23, 60.18) * mm, v(96.89, 57.9) * mm, v(96.32, 55.51) * mm, v(95.65, 53.3) * mm, v(95.25, 52) * mm], "startDerivative": vector(6.69, -19.51) * mm, "endDerivative": vector(-4.6, -12.75) * mm});
            skLineSegment(sketch, "E66.MirrorCS", {"start": v(88.59, 59.05) * mm, "end": v(81.98, 55.18) * mm});
            skFitSpline(sketch, "E67.MirrorCS", {"points": [v(102.03, 88.6) * mm, v(100.8, 85.4) * mm, v(102.15, 81.66) * mm, v(104.34, 79.03) * mm, v(104.81, 77.49) * mm, v(104.76, 75.8) * mm, v(104.36, 73.57) * mm], "startDerivative": vector(-15.35, -14.7) * mm, "endDerivative": vector(-4.08, -12.06) * mm});
            skFitSpline(sketch, "E68.MirrorCS", {"points": [v(95.25, 52) * mm, v(96.4, 52.94) * mm, v(98.67, 56.48) * mm, v(99.74, 59.9) * mm, v(99.84, 63.32) * mm, v(99.17, 66.64) * mm, v(97.73, 69.26) * mm, v(96.37, 71) * mm, v(95.24, 72) * mm], "startDerivative": vector(13.48, 8.73) * mm, "endDerivative": vector(-15.01, 11.43) * mm});
            skSolve(sketch);
        }
        {
            var Q0;
            Q0 = qSketchRegion(id + "F15", true);
            extrude(context, id + "F16", {"entities" : qUnion([Q0]), "operationType" : NewBodyOperationType.REMOVE, "oppositeDirection" : true, "depth" : (getVariable(context, 'depthLion')) * mm, "offsetDistance" : 25.4 * mm});
        }
    });
